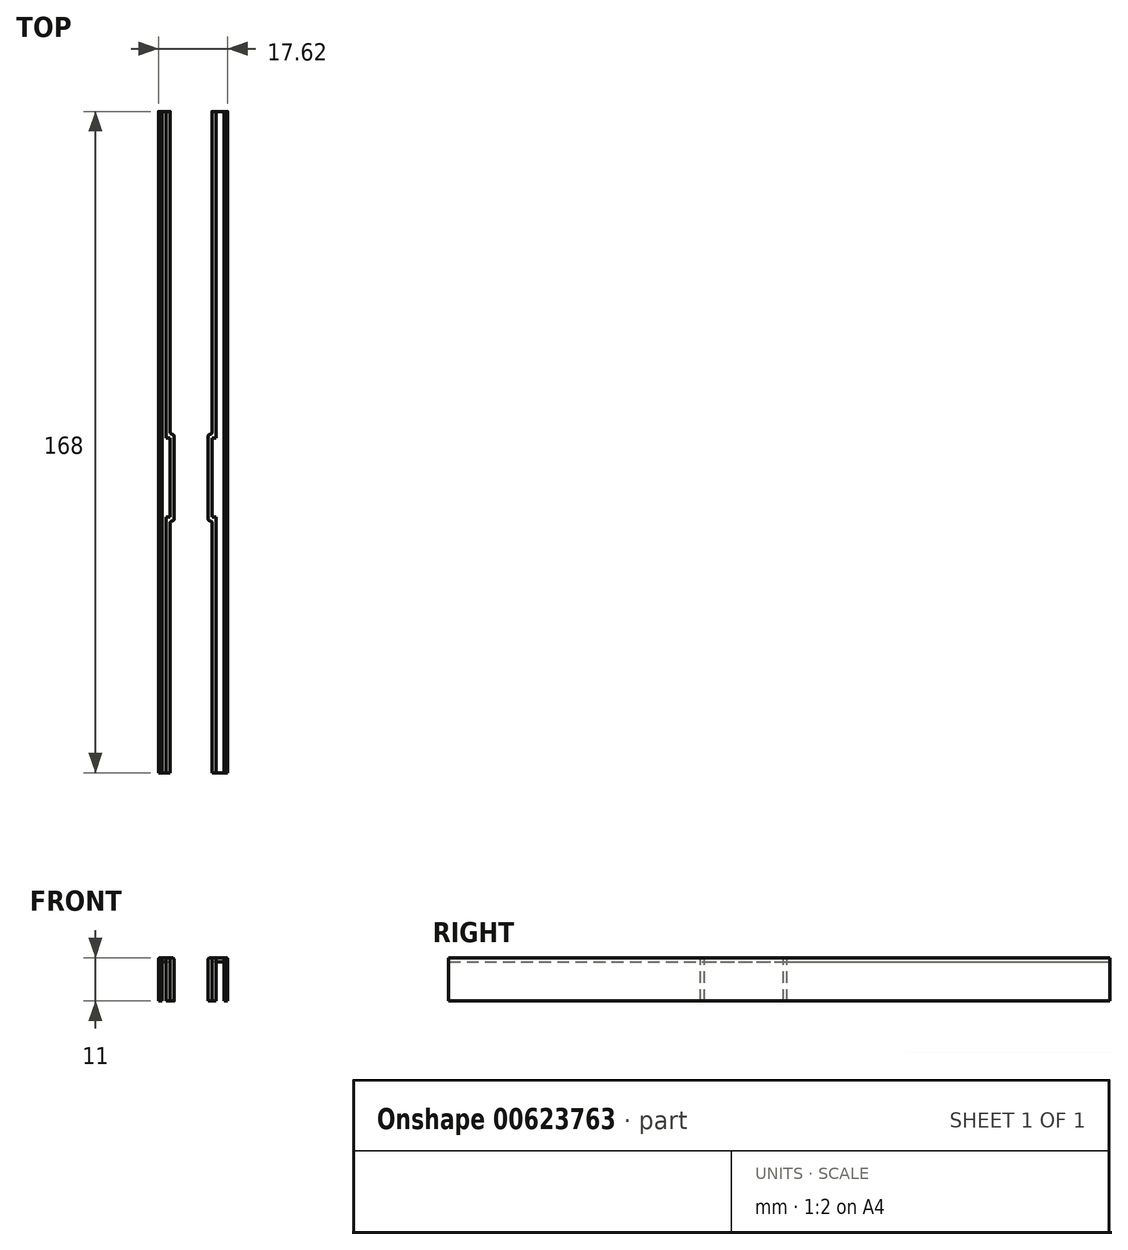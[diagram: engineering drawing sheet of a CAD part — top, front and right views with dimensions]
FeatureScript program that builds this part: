
annotation { "Feature Type Name" : "Feature", "Feature Type Description" : "" }
export const myFeature = defineFeature(function(context is Context, id is Id, definition is map)
    precondition{}
    {
        {
            var Q0;
            Q0=qCreatedBy(makeId("Top.planeOp"),FACE);
            var sketch = newSketch(context, id + "F0", { "sketchPlane" : qUnion([Q0])});
            skLineSegment(sketch, "E0.bottom", {"start": v(0, 0) * mm, "end": v(-1, 0) * mm});
            skLineSegment(sketch, "E0.top", {"start": v(0, 168) * mm, "end": v(-1, 168) * mm});
            skLineSegment(sketch, "E0.left", {"start": v(0, 0) * mm, "end": v(0, 168) * mm});
            skLineSegment(sketch, "E0.right", {"start": v(-1, 0) * mm, "end": v(-1, 168) * mm});
            skLineSegment(sketch, "E1.bottom", {"start": v(-1, 0) * mm, "end": v(-2, 0) * mm});
            skLineSegment(sketch, "E1.top", {"start": v(-1, 168) * mm, "end": v(-2, 168) * mm});
            skLineSegment(sketch, "E1.right", {"start": v(-2, 0) * mm, "end": v(-2, 168) * mm});
            skLineSegment(sketch, "E2.bottom", {"start": v(0, 0) * mm, "end": v(1, 0) * mm});
            skLineSegment(sketch, "E2.top", {"start": v(0, 168) * mm, "end": v(1, 168) * mm});
            skLineSegment(sketch, "E2.right", {"start": v(1, 0) * mm, "end": v(1, 168) * mm});
            skLineSegment(sketch, "E3.bottom", {"start": v(0, 65) * mm, "end": v(1, 65) * mm});
            skLineSegment(sketch, "E3.top", {"start": v(0, 85) * mm, "end": v(1, 85) * mm});
            skLineSegment(sketch, "E3.left", {"start": v(0, 65) * mm, "end": v(0, 85) * mm});
            skLineSegment(sketch, "E3.right", {"start": v(1, 65) * mm, "end": v(1, 85) * mm});
            skLineSegment(sketch, "E4", {"start": v(1, 65) * mm, "end": v(1, 0) * mm, "construction": true});
            skLineSegment(sketch, "E5.bottom", {"start": v(1, 64) * mm, "end": v(2, 64) * mm});
            skLineSegment(sketch, "E5.top", {"start": v(1, 86) * mm, "end": v(2, 86) * mm});
            skLineSegment(sketch, "E5.left", {"start": v(1, 64) * mm, "end": v(1, 86) * mm});
            skLineSegment(sketch, "E5.right", {"start": v(2, 64) * mm, "end": v(2, 86) * mm});
            skLineSegment(sketch, "E6", {"start": v(1, 65) * mm, "end": v(1, 64) * mm, "construction": true});
            skLineSegment(sketch, "E7.bottom", {"start": v(12.62, 0) * mm, "end": v(14.62, 0) * mm});
            skLineSegment(sketch, "E7.top", {"start": v(12.62, 168) * mm, "end": v(14.62, 168) * mm});
            skLineSegment(sketch, "E7.left", {"start": v(12.62, 0) * mm, "end": v(12.62, 168) * mm});
            skLineSegment(sketch, "E7.right", {"start": v(14.62, 0) * mm, "end": v(14.62, 168) * mm});
            skLineSegment(sketch, "E8.bottom", {"start": v(12.62, 0) * mm, "end": v(11.62, 0) * mm});
            skLineSegment(sketch, "E8.top", {"start": v(12.62, 168) * mm, "end": v(11.62, 168) * mm});
            skLineSegment(sketch, "E8.right", {"start": v(11.62, 0) * mm, "end": v(11.62, 168) * mm});
            skLineSegment(sketch, "E9.bottom", {"start": v(14.62, 0) * mm, "end": v(15.62, 0) * mm});
            skLineSegment(sketch, "E9.top", {"start": v(14.62, 168) * mm, "end": v(15.62, 168) * mm});
            skLineSegment(sketch, "E9.right", {"start": v(15.62, 0) * mm, "end": v(15.62, 168) * mm});
            skLineSegment(sketch, "E10.bottom", {"start": v(12.62, 65) * mm, "end": v(11.62, 65) * mm});
            skLineSegment(sketch, "E10.top", {"start": v(12.62, 85) * mm, "end": v(11.62, 85) * mm});
            skLineSegment(sketch, "E10.left", {"start": v(12.62, 65) * mm, "end": v(12.62, 85) * mm});
            skLineSegment(sketch, "E10.right", {"start": v(11.62, 65) * mm, "end": v(11.62, 85) * mm});
            skLineSegment(sketch, "E11.bottom", {"start": v(11.62, 64) * mm, "end": v(10.62, 64) * mm});
            skLineSegment(sketch, "E11.top", {"start": v(11.62, 86) * mm, "end": v(10.62, 86) * mm});
            skLineSegment(sketch, "E11.left", {"start": v(11.62, 64) * mm, "end": v(11.62, 86) * mm});
            skLineSegment(sketch, "E11.right", {"start": v(10.62, 64) * mm, "end": v(10.62, 86) * mm});
            skSolve(sketch);
        }
        {
            var Q0;
            {var subQ1=sQuery(id+"F0.wireOp",EDGE,"E0.bottom");Q0=makeQuery(id+"F0.imprint","IMPRINT",FACE,{"disambiguationData":[TD([[makeQuery(id+"F0.imprint","IMPRINT",EDGE,{"derivedFrom":subQ1}),-1.0]])]});}
            var Q1;
            {var subQ0=sQuery(id+"F0.wireOp",EDGE,"E3.bottom");Q1=makeQuery(id+"F0.imprint","IMPRINT",FACE,{"disambiguationData":[TD([[makeQuery(id+"F0.imprint","IMPRINT",EDGE,{"derivedFrom":subQ0}),1.0]])]});}
            var Q2;
            {var subQ1=sQuery(id+"F0.wireOp",EDGE,"E7.bottom");Q2=makeQuery(id+"F0.imprint","IMPRINT",FACE,{"disambiguationData":[TD([[makeQuery(id+"F0.imprint","IMPRINT",EDGE,{"derivedFrom":subQ1}),1.0]])]});}
            var Q3;
            {var subQ0=sQuery(id+"F0.wireOp",EDGE,"E10.bottom");Q3=makeQuery(id+"F0.imprint","IMPRINT",FACE,{"disambiguationData":[TD([[makeQuery(id+"F0.imprint","IMPRINT",EDGE,{"derivedFrom":subQ0}),-1.0]])]});}
            extrude(context, id + "F1", {"entities" : qUnion([Q0, Q1, Q2, Q3]), "oppositeDirection" : true, "depth" : 1 * mm, "offsetDistance" : 25 * mm});
        }
        {
            var Q0;
            Q0=makeQuery(id+"F0.imprint","IMPRINT",FACE,{"disambiguationData":[TD([[makeQuery(id+"F0.imprint","IMPRINT",EDGE,{"derivedFrom":sQuery(id+"F0.wireOp",EDGE,"E1.bottom")}),-1.0]])]});
            var Q1;
            {var subQ2=sQuery(id+"F0.wireOp",EDGE,"E2.top");Q1=makeQuery(id+"F0.imprint","IMPRINT",FACE,{"disambiguationData":[TD([[makeQuery(id+"F0.imprint","IMPRINT",EDGE,{"derivedFrom":subQ2}),-1.0]])]});}
            var Q2;
            {var subQ3=sQuery(id+"F0.wireOp",EDGE,"E5.bottom");Q2=makeQuery(id+"F0.imprint","IMPRINT",FACE,{"disambiguationData":[TD([[makeQuery(id+"F0.imprint","IMPRINT",EDGE,{"derivedFrom":subQ3}),1.0]])]});}
            var Q3;
            {var subQ2=sQuery(id+"F0.wireOp",EDGE,"E2.bottom");Q3=makeQuery(id+"F0.imprint","IMPRINT",FACE,{"disambiguationData":[TD([[makeQuery(id+"F0.imprint","IMPRINT",EDGE,{"derivedFrom":subQ2}),1.0]])]});}
            var Q4;
            {var subQ3=sQuery(id+"F0.wireOp",EDGE,"E11.bottom");Q4=makeQuery(id+"F0.imprint","IMPRINT",FACE,{"disambiguationData":[TD([[makeQuery(id+"F0.imprint","IMPRINT",EDGE,{"derivedFrom":subQ3}),-1.0]])]});}
            var Q5;
            {var subQ1=sQuery(id+"F0.wireOp",EDGE,"E8.bottom");Q5=makeQuery(id+"F0.imprint","IMPRINT",FACE,{"disambiguationData":[TD([[makeQuery(id+"F0.imprint","IMPRINT",EDGE,{"derivedFrom":subQ1}),-1.0]])]});}
            var Q6;
            {var subQ1=sQuery(id+"F0.wireOp",EDGE,"E8.top");Q6=makeQuery(id+"F0.imprint","IMPRINT",FACE,{"disambiguationData":[TD([[makeQuery(id+"F0.imprint","IMPRINT",EDGE,{"derivedFrom":subQ1}),1.0]])]});}
            var Q7;
            Q7=makeQuery(id+"F0.imprint","IMPRINT",FACE,{"disambiguationData":[TD([[makeQuery(id+"F0.imprint","IMPRINT",EDGE,{"derivedFrom":sQuery(id+"F0.wireOp",EDGE,"E9.bottom")}),1.0]])]});
            extrude(context, id + "F2", {"entities" : qUnion([Q0, Q1, Q2, Q3, Q4, Q5, Q6, Q7]), "oppositeDirection" : true, "depth" : 11 * mm, "offsetDistance" : 25 * mm});
        }
        {
            var Q0;
            Q0=makeQuery(id+"F2.opExtrude","CAP_EDGE",EDGE,{"disambiguationData":[OSD([sQuery(id+"F0.wireOp",EDGE,"E9.right")])],"isStart":true});
            var Q1;
            {var subQ0=sQuery(id+"F0.wireOp",EDGE,"E8.right");Q1=makeQuery(id+"F2.opExtrude","CAP_EDGE",EDGE,{"disambiguationData":[OSD([subQ0]),TDD([makeQuery(id+"F0.imprint","IMPRINT",EDGE,{"disambiguationData":[TD([[makeQuery(id+"F0.imprint","INTERSECT",VERTEX,{"derivedFrom":[sQuery(id+"F0.wireOp",EDGE,"E8.bottom"),subQ0]}),-1.0]])],"derivedFrom":subQ0})])],"isStart":true});}
            var Q2;
            {var subQ0=sQuery(id+"F0.wireOp",EDGE,"E2.right");Q2=makeQuery(id+"F2.opExtrude","CAP_EDGE",EDGE,{"disambiguationData":[OSD([subQ0]),TDD([makeQuery(id+"F0.imprint","IMPRINT",EDGE,{"disambiguationData":[TD([[makeQuery(id+"F0.imprint","INTERSECT",VERTEX,{"derivedFrom":[sQuery(id+"F0.wireOp",EDGE,"E2.bottom"),subQ0]}),-1.0]])],"derivedFrom":subQ0})])],"isStart":true});}
            var Q3;
            Q3=makeQuery(id+"F2.opExtrude","CAP_EDGE",EDGE,{"disambiguationData":[OSD([sQuery(id+"F0.wireOp",EDGE,"E1.right")])],"isStart":true});
            var Q4;
            Q4=makeQuery(id+"F2.opExtrude","CAP_EDGE",EDGE,{"disambiguationData":[OSD([sQuery(id+"F0.wireOp",EDGE,"E11.right")])],"isStart":true});
            var Q5;
            Q5=makeQuery(id+"F2.opExtrude","CAP_EDGE",EDGE,{"disambiguationData":[OSD([sQuery(id+"F0.wireOp",EDGE,"E5.right")])],"isStart":true});
            var Q6;
            {var subQ0=sQuery(id+"F0.wireOp",EDGE,"E8.right");Q6=makeQuery(id+"F2.opExtrude","CAP_EDGE",EDGE,{"disambiguationData":[OSD([subQ0]),TDD([makeQuery(id+"F0.imprint","IMPRINT",EDGE,{"disambiguationData":[TD([[makeQuery(id+"F0.imprint","INTERSECT",VERTEX,{"derivedFrom":[sQuery(id+"F0.wireOp",EDGE,"E8.top"),subQ0]}),1.0]])],"derivedFrom":subQ0})])],"isStart":true});}
            var Q7;
            {var subQ0=sQuery(id+"F0.wireOp",EDGE,"E2.right");Q7=makeQuery(id+"F2.opExtrude","CAP_EDGE",EDGE,{"disambiguationData":[OSD([subQ0]),TDD([makeQuery(id+"F0.imprint","IMPRINT",EDGE,{"disambiguationData":[TD([[makeQuery(id+"F0.imprint","INTERSECT",VERTEX,{"derivedFrom":[sQuery(id+"F0.wireOp",EDGE,"E2.top"),subQ0]}),1.0]])],"derivedFrom":subQ0})])],"isStart":true});}
            var Q8;
            Q8=makeQuery(id+"F2.opExtrude","CAP_EDGE",EDGE,{"disambiguationData":[OSD([sQuery(id+"F0.wireOp",EDGE,"E5.top")])],"isStart":true});
            var Q9;
            Q9=makeQuery(id+"F2.opExtrude","CAP_EDGE",EDGE,{"disambiguationData":[OSD([sQuery(id+"F0.wireOp",EDGE,"E11.top")])],"isStart":true});
            var Q10;
            Q10=makeQuery(id+"F2.opExtrude","CAP_EDGE",EDGE,{"disambiguationData":[OSD([sQuery(id+"F0.wireOp",EDGE,"E11.bottom")])],"isStart":true});
            var Q11;
            Q11=makeQuery(id+"F2.opExtrude","CAP_EDGE",EDGE,{"disambiguationData":[OSD([sQuery(id+"F0.wireOp",EDGE,"E5.bottom")])],"isStart":true});
            var Q12;
            Q12=makeQuery(id+"F2.opExtrude","SWEPT_EDGE",EDGE,{"disambiguationData":[OSD([sQuery(id+"F0.wireOp",EDGE,"E5.bottom"),sQuery(id+"F0.wireOp",EDGE,"E5.right")])]});
            var Q13;
            Q13=makeQuery(id+"F2.opExtrude","SWEPT_EDGE",EDGE,{"disambiguationData":[OSD([sQuery(id+"F0.wireOp",EDGE,"E11.bottom"),sQuery(id+"F0.wireOp",EDGE,"E11.right")])]});
            var Q14;
            Q14=makeQuery(id+"F2.opExtrude","SWEPT_EDGE",EDGE,{"disambiguationData":[OSD([sQuery(id+"F0.wireOp",EDGE,"E5.top"),sQuery(id+"F0.wireOp",EDGE,"E5.right")])]});
            var Q15;
            Q15=makeQuery(id+"F2.opExtrude","SWEPT_EDGE",EDGE,{"disambiguationData":[OSD([sQuery(id+"F0.wireOp",EDGE,"E11.top"),sQuery(id+"F0.wireOp",EDGE,"E11.right")])]});
            var Q16;
            Q16=makeQuery(id+"F2.opExtrude","SWEPT_EDGE",EDGE,{"disambiguationData":[OSD([sQuery(id+"F0.wireOp",EDGE,"E8.right"),sQuery(id+"F0.wireOp",EDGE,"E11.top"),sQuery(id+"F0.wireOp",EDGE,"E11.left")])]});
            var Q17;
            Q17=makeQuery(id+"F2.opExtrude","SWEPT_EDGE",EDGE,{"disambiguationData":[OSD([sQuery(id+"F0.wireOp",EDGE,"E2.right"),sQuery(id+"F0.wireOp",EDGE,"E5.top"),sQuery(id+"F0.wireOp",EDGE,"E5.left")])]});
            var Q18;
            Q18=makeQuery(id+"F2.opExtrude","SWEPT_EDGE",EDGE,{"disambiguationData":[OSD([sQuery(id+"F0.wireOp",EDGE,"E8.right"),sQuery(id+"F0.wireOp",EDGE,"E11.bottom"),sQuery(id+"F0.wireOp",EDGE,"E11.left")])]});
            var Q19;
            Q19=makeQuery(id+"F2.opExtrude","SWEPT_EDGE",EDGE,{"disambiguationData":[OSD([sQuery(id+"F0.wireOp",EDGE,"E2.right"),sQuery(id+"F0.wireOp",EDGE,"E5.bottom"),sQuery(id+"F0.wireOp",EDGE,"E5.left")])]});
            fillet(context, id + "F3", {"entities" : qUnion([Q0, Q1, Q2, Q3, Q4, Q5, Q6, Q7, Q8, Q9, Q10, Q11, Q12, Q13, Q14, Q15, Q16, Q17, Q18, Q19]), "radius" : .5 * mm, "tangentPropagation" : true, "allowEdgeOverflow" : false});
        }
    });
